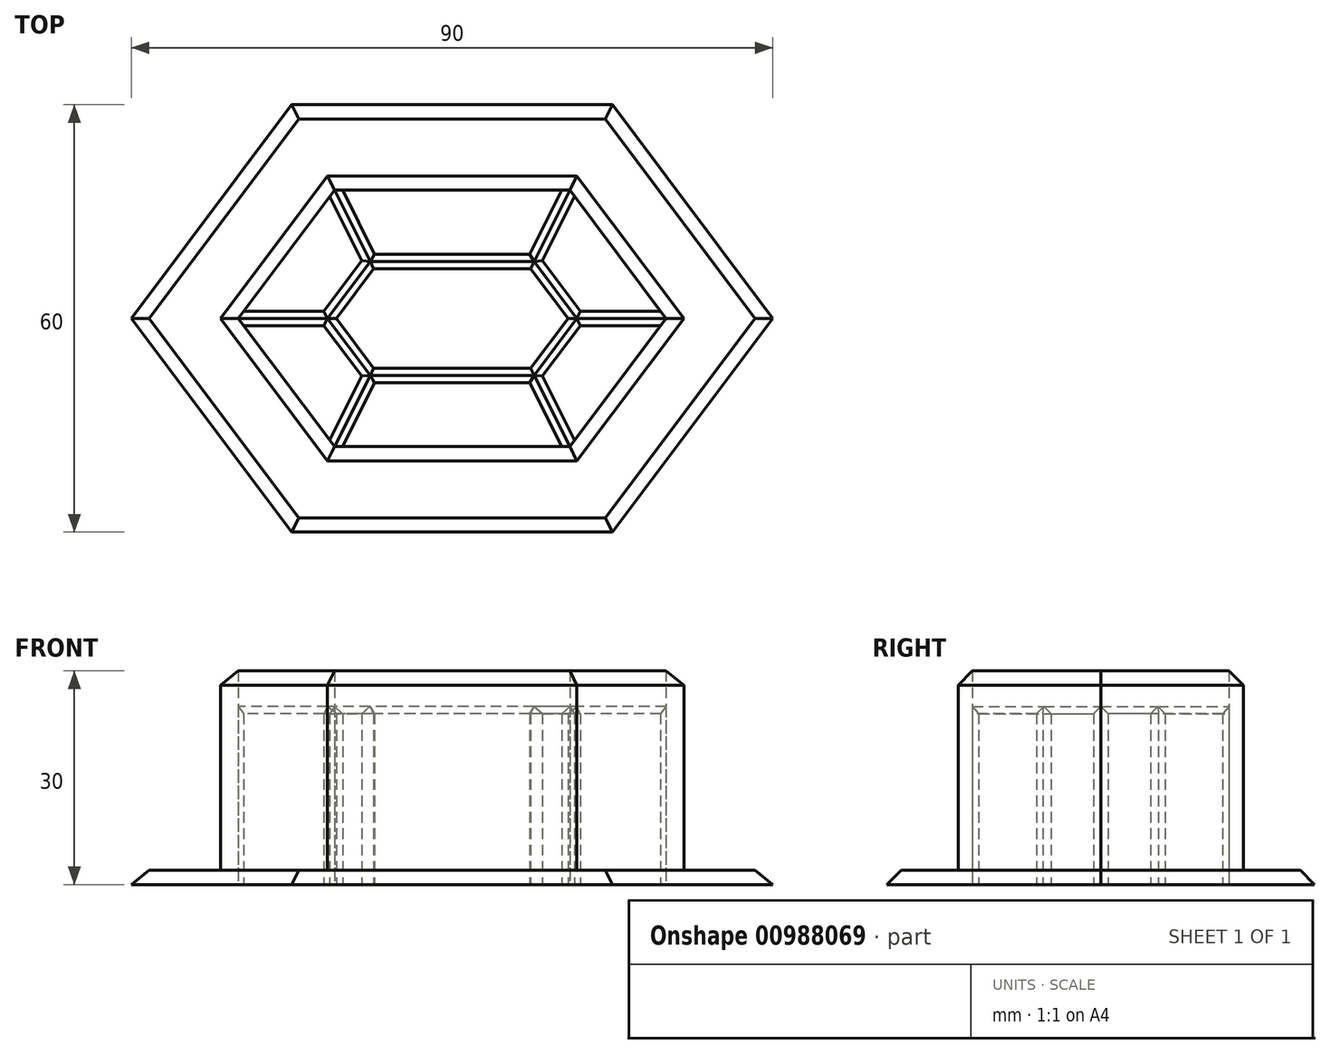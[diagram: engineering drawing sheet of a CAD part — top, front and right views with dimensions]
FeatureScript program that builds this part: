
annotation { "Feature Type Name" : "Feature", "Feature Type Description" : "" }
export const myFeature = defineFeature(function(context is Context, id is Id, definition is map)
    precondition{}
    {
        {
            var Q0;
            Q0=qCreatedBy(makeId("Top.planeOp"),FACE);
            var sketch = newSketch(context, id + "F0", { "sketchPlane" : qUnion([Q0])});
            skLineSegment(sketch, "E0", {"start": v(-17.5, 20) * mm, "end": v(17.5, 20) * mm});
            skLineSegment(sketch, "E1", {"start": v(17.5, 20) * mm, "end": v(32.5, 0) * mm});
            skLineSegment(sketch, "E2", {"start": v(32.5, 0) * mm, "end": v(17.5, -20) * mm});
            skLineSegment(sketch, "E3", {"start": v(17.5, -20) * mm, "end": v(-17.5, -20) * mm});
            skLineSegment(sketch, "E4", {"start": v(-17.5, -20) * mm, "end": v(-32.5, 0) * mm});
            skLineSegment(sketch, "E5", {"start": v(-32.5, 0) * mm, "end": v(-17.5, 20) * mm});
            skLineSegment(sketch, "E6", {"start": v(-32.5, 0) * mm, "end": v(32.5, 0) * mm, "construction": true});
            skLineSegment(sketch, "E7", {"start": v(0, 0) * mm, "end": v(0, 20) * mm, "construction": true});
            skLineSegment(sketch, "E8", {"start": v(0, 0) * mm, "end": v(0, -20) * mm, "construction": true});
            skLineSegment(sketch, "E9.0", {"start": v(-16.5, -18) * mm, "end": v(-30, 0) * mm});
            skLineSegment(sketch, "E9.1", {"start": v(-16.5, 18) * mm, "end": v(16.5, 18) * mm});
            skLineSegment(sketch, "E9.2", {"start": v(16.5, 18) * mm, "end": v(30, 0) * mm});
            skLineSegment(sketch, "E9.3", {"start": v(-30, 0) * mm, "end": v(-16.5, 18) * mm});
            skLineSegment(sketch, "E9.4", {"start": v(30, 0) * mm, "end": v(16.5, -18) * mm});
            skLineSegment(sketch, "E9.5", {"start": v(16.5, -18) * mm, "end": v(-16.5, -18) * mm});
            skLineSegment(sketch, "E10.0", {"start": v(-22.5, -30) * mm, "end": v(-45, 0) * mm});
            skLineSegment(sketch, "E10.1", {"start": v(-22.5, 30) * mm, "end": v(22.5, 30) * mm});
            skLineSegment(sketch, "E10.2", {"start": v(22.5, 30) * mm, "end": v(45, 0) * mm});
            skLineSegment(sketch, "E10.3", {"start": v(-45, 0) * mm, "end": v(-22.5, 30) * mm});
            skLineSegment(sketch, "E10.4", {"start": v(45, 0) * mm, "end": v(22.5, -30) * mm});
            skLineSegment(sketch, "E10.5", {"start": v(22.5, -30) * mm, "end": v(-22.5, -30) * mm});
            skSolve(sketch);
        }
        {
            var Q0;
            Q0=makeQuery(id+"F0.imprint","IMPRINT",FACE,{"disambiguationData":[TD([[makeQuery(id+"F0.imprint","IMPRINT",EDGE,{"derivedFrom":sQuery(id+"F0.wireOp",EDGE,"E0")}),-1.0]])]});
            extrude(context, id + "F1", {"entities" : qUnion([Q0]), "depth" : 30 * mm, "offsetDistance" : 25 * mm});
        }
        {
            var Q0;
            Q0=makeQuery(id+"F0.imprint","IMPRINT",FACE,{"disambiguationData":[TD([[makeQuery(id+"F0.imprint","IMPRINT",EDGE,{"derivedFrom":sQuery(id+"F0.wireOp",EDGE,"E0")}),1.0]])]});
            extrude(context, id + "F2", {"entities" : qUnion([Q0]), "operationType" : NewBodyOperationType.ADD, "depth" : 2 * mm, "offsetDistance" : 25 * mm});
        }
        {
            var Q0;
            Q0=makeQuery(id+"F1.opExtrude","CAP_EDGE",EDGE,{"disambiguationData":[OSD([sQuery(id+"F0.wireOp",EDGE,"E5")])],"isStart":false});
            var Q1;
            Q1=makeQuery(id+"F1.opExtrude","CAP_EDGE",EDGE,{"disambiguationData":[OSD([sQuery(id+"F0.wireOp",EDGE,"E0")])],"isStart":false});
            var Q2;
            Q2=makeQuery(id+"F1.opExtrude","CAP_EDGE",EDGE,{"disambiguationData":[OSD([sQuery(id+"F0.wireOp",EDGE,"E1")])],"isStart":false});
            var Q3;
            Q3=makeQuery(id+"F1.opExtrude","CAP_EDGE",EDGE,{"disambiguationData":[OSD([sQuery(id+"F0.wireOp",EDGE,"E2")])],"isStart":false});
            var Q4;
            Q4=makeQuery(id+"F1.opExtrude","CAP_EDGE",EDGE,{"disambiguationData":[OSD([sQuery(id+"F0.wireOp",EDGE,"E3")])],"isStart":false});
            var Q5;
            Q5=makeQuery(id+"F1.opExtrude","CAP_EDGE",EDGE,{"disambiguationData":[OSD([sQuery(id+"F0.wireOp",EDGE,"E4")])],"isStart":false});
            var Q6;
            Q6=makeQuery(id+"F2.opExtrude","CAP_EDGE",EDGE,{"disambiguationData":[OSD([sQuery(id+"F0.wireOp",EDGE,"E10.5")])],"isStart":false});
            var Q7;
            Q7=makeQuery(id+"F2.opExtrude","CAP_EDGE",EDGE,{"disambiguationData":[OSD([sQuery(id+"F0.wireOp",EDGE,"E10.4")])],"isStart":false});
            var Q8;
            Q8=makeQuery(id+"F2.opExtrude","CAP_EDGE",EDGE,{"disambiguationData":[OSD([sQuery(id+"F0.wireOp",EDGE,"E10.2")])],"isStart":false});
            var Q9;
            Q9=makeQuery(id+"F2.opExtrude","CAP_EDGE",EDGE,{"disambiguationData":[OSD([sQuery(id+"F0.wireOp",EDGE,"E10.0")])],"isStart":false});
            var Q10;
            Q10=makeQuery(id+"F2.opExtrude","CAP_EDGE",EDGE,{"disambiguationData":[OSD([sQuery(id+"F0.wireOp",EDGE,"E10.3")])],"isStart":false});
            var Q11;
            Q11=makeQuery(id+"F2.opExtrude","CAP_EDGE",EDGE,{"disambiguationData":[OSD([sQuery(id+"F0.wireOp",EDGE,"E10.1")])],"isStart":false});
            chamfer(context, id + "F3", {"entities" : qUnion([Q0, Q1, Q2, Q3, Q4, Q5, Q6, Q7, Q8, Q9, Q10, Q11]), "width" : 2 * mm, "tangentPropagation" : true});
        }
        {
            var Q0;
            Q0=qCreatedBy(makeId("Top.planeOp"),FACE);
            var sketch = newSketch(context, id + "F4", { "sketchPlane" : qUnion([Q0])});
            skLineSegment(sketch, "E11", {"start": v(-32.5, 0) * mm, "end": v(-17.5, 20) * mm});
            skLineSegment(sketch, "E12", {"start": v(-17.5, 20) * mm, "end": v(17.5, 20) * mm});
            skLineSegment(sketch, "E13", {"start": v(17.5, 20) * mm, "end": v(32.5, 0) * mm});
            skLineSegment(sketch, "E14", {"start": v(32.5, 0) * mm, "end": v(17.5, -20) * mm});
            skLineSegment(sketch, "E15", {"start": v(17.5, -20) * mm, "end": v(-17.5, -20) * mm});
            skLineSegment(sketch, "E16", {"start": v(-17.5, -20) * mm, "end": v(-32.5, 0) * mm});
            skLineSegment(sketch, "E17.0", {"start": v(-16.5, -18) * mm, "end": v(-30, 0) * mm});
            skLineSegment(sketch, "E17.1", {"start": v(-16.5, 18) * mm, "end": v(16.5, 18) * mm});
            skLineSegment(sketch, "E17.2", {"start": v(16.5, 18) * mm, "end": v(30, 0) * mm});
            skLineSegment(sketch, "E17.3", {"start": v(-30, 0) * mm, "end": v(-16.5, 18) * mm});
            skLineSegment(sketch, "E17.4", {"start": v(30, 0) * mm, "end": v(16.5, -18) * mm});
            skLineSegment(sketch, "E17.5", {"start": v(16.5, -18) * mm, "end": v(-16.5, -18) * mm});
            skLineSegment(sketch, "E18.0", {"start": v(-11.5, -8) * mm, "end": v(-17.5, 0) * mm, "construction": true});
            skLineSegment(sketch, "E18.1", {"start": v(-11.5, 8) * mm, "end": v(11.5, 8) * mm, "construction": true});
            skLineSegment(sketch, "E18.2", {"start": v(11.5, 8) * mm, "end": v(17.5, 0) * mm, "construction": true});
            skLineSegment(sketch, "E18.3", {"start": v(-17.5, 0) * mm, "end": v(-11.5, 8) * mm, "construction": true});
            skLineSegment(sketch, "E18.4", {"start": v(17.5, 0) * mm, "end": v(11.5, -8) * mm, "construction": true});
            skLineSegment(sketch, "E18.5", {"start": v(11.5, -8) * mm, "end": v(-11.5, -8) * mm, "construction": true});
            skLineSegment(sketch, "E19", {"start": v(-11.5, 8) * mm, "end": v(-16.5, 18) * mm, "construction": true});
            skLineSegment(sketch, "E20", {"start": v(11.5, 8) * mm, "end": v(16.5, 18) * mm, "construction": true});
            skLineSegment(sketch, "E21", {"start": v(17.5, 0) * mm, "end": v(30, 0) * mm, "construction": true});
            skLineSegment(sketch, "E22", {"start": v(11.5, -8) * mm, "end": v(16.5, -18) * mm, "construction": true});
            skLineSegment(sketch, "E23", {"start": v(-11.5, -8) * mm, "end": v(-16.5, -18) * mm, "construction": true});
            skLineSegment(sketch, "E24", {"start": v(-17.5, 0) * mm, "end": v(-30, 0) * mm, "construction": true});
            skLineSegment(sketch, "E25.0", {"start": v(-12.67, 8.1) * mm, "end": v(-17.17, 17.1) * mm});
            skLineSegment(sketch, "E25.1", {"start": v(-18, 1) * mm, "end": v(-12.67, 8.1) * mm});
            skLineSegment(sketch, "E25.2", {"start": v(-18, 1) * mm, "end": v(-29.25, 1) * mm});
            skLineSegment(sketch, "E26.0", {"start": v(-10.88, 9) * mm, "end": v(-15.38, 18) * mm});
            skLineSegment(sketch, "E26.1", {"start": v(-10.88, 9) * mm, "end": v(10.88, 9) * mm});
            skLineSegment(sketch, "E26.2", {"start": v(10.88, 9) * mm, "end": v(15.38, 18) * mm});
            skLineSegment(sketch, "E27.0", {"start": v(18, 1) * mm, "end": v(29.25, 1) * mm});
            skLineSegment(sketch, "E27.1", {"start": v(12.67, 8.1) * mm, "end": v(18, 1) * mm});
            skLineSegment(sketch, "E27.2", {"start": v(12.67, 8.1) * mm, "end": v(17.17, 17.1) * mm});
            skLineSegment(sketch, "E28.0", {"start": v(18, -1) * mm, "end": v(29.25, -1) * mm});
            skLineSegment(sketch, "E28.1", {"start": v(18, -1) * mm, "end": v(12.67, -8.1) * mm});
            skLineSegment(sketch, "E28.2", {"start": v(12.67, -8.1) * mm, "end": v(17.17, -17.1) * mm});
            skLineSegment(sketch, "E29.0", {"start": v(-10.88, -9) * mm, "end": v(-15.38, -18) * mm});
            skLineSegment(sketch, "E29.1", {"start": v(10.88, -9) * mm, "end": v(-10.88, -9) * mm});
            skLineSegment(sketch, "E29.2", {"start": v(10.88, -9) * mm, "end": v(15.38, -18) * mm});
            skLineSegment(sketch, "E30.0", {"start": v(-12.67, -8.1) * mm, "end": v(-17.17, -17.1) * mm});
            skLineSegment(sketch, "E30.1", {"start": v(-12.67, -8.1) * mm, "end": v(-18, -1) * mm});
            skLineSegment(sketch, "E30.2", {"start": v(-18, -1) * mm, "end": v(-29.25, -1) * mm});
            skLineSegment(sketch, "E31.0", {"start": v(-16.25, 0) * mm, "end": v(-11, 7) * mm});
            skLineSegment(sketch, "E31.1", {"start": v(11, 7) * mm, "end": v(16.25, 0) * mm});
            skLineSegment(sketch, "E31.2", {"start": v(16.25, 0) * mm, "end": v(11, -7) * mm});
            skLineSegment(sketch, "E31.3", {"start": v(-11, 7) * mm, "end": v(11, 7) * mm});
            skLineSegment(sketch, "E31.4", {"start": v(11, -7) * mm, "end": v(-11, -7) * mm});
            skLineSegment(sketch, "E31.5", {"start": v(-11, -7) * mm, "end": v(-16.25, 0) * mm});
            skSolve(sketch);
        }
        {
            var Q0;
            {var subQ4=sQuery(id+"F4.wireOp",EDGE,"E25.0");Q0=makeQuery(id+"F4.imprint","IMPRINT",FACE,{"disambiguationData":[TD([[makeQuery(id+"F4.imprint","IMPRINT",EDGE,{"derivedFrom":subQ4}),-1.0]])]});}
            extrude(context, id + "F5", {"entities" : qUnion([Q0]), "depth" : 25 * mm, "offsetDistance" : 25 * mm});
        }
        {
            var Q0;
            Q0=makeQuery(id+"F5.opExtrude","CAP_EDGE",EDGE,{"disambiguationData":[OSD([sQuery(id+"F4.wireOp",EDGE,"E30.2")])],"isStart":false});
            var Q1;
            Q1=makeQuery(id+"F5.opExtrude","CAP_EDGE",EDGE,{"disambiguationData":[OSD([sQuery(id+"F4.wireOp",EDGE,"E25.2")])],"isStart":false});
            var Q2;
            Q2=makeQuery(id+"F5.opExtrude","CAP_EDGE",EDGE,{"disambiguationData":[OSD([sQuery(id+"F4.wireOp",EDGE,"E30.1")])],"isStart":false});
            var Q3;
            Q3=makeQuery(id+"F5.opExtrude","CAP_EDGE",EDGE,{"disambiguationData":[OSD([sQuery(id+"F4.wireOp",EDGE,"E31.5")])],"isStart":false});
            var Q4;
            Q4=makeQuery(id+"F5.opExtrude","CAP_EDGE",EDGE,{"disambiguationData":[OSD([sQuery(id+"F4.wireOp",EDGE,"E31.0")])],"isStart":false});
            var Q5;
            Q5=makeQuery(id+"F5.opExtrude","CAP_EDGE",EDGE,{"disambiguationData":[OSD([sQuery(id+"F4.wireOp",EDGE,"E25.1")])],"isStart":false});
            var Q6;
            Q6=makeQuery(id+"F5.opExtrude","CAP_EDGE",EDGE,{"disambiguationData":[OSD([sQuery(id+"F4.wireOp",EDGE,"E25.0")])],"isStart":false});
            var Q7;
            Q7=makeQuery(id+"F5.opExtrude","CAP_EDGE",EDGE,{"disambiguationData":[OSD([sQuery(id+"F4.wireOp",EDGE,"E26.0")])],"isStart":false});
            var Q8;
            Q8=makeQuery(id+"F5.opExtrude","CAP_EDGE",EDGE,{"disambiguationData":[OSD([sQuery(id+"F4.wireOp",EDGE,"E31.3")])],"isStart":false});
            var Q9;
            Q9=makeQuery(id+"F5.opExtrude","CAP_EDGE",EDGE,{"disambiguationData":[OSD([sQuery(id+"F4.wireOp",EDGE,"E26.1")])],"isStart":false});
            var Q10;
            Q10=makeQuery(id+"F5.opExtrude","CAP_EDGE",EDGE,{"disambiguationData":[OSD([sQuery(id+"F4.wireOp",EDGE,"E29.1")])],"isStart":false});
            var Q11;
            Q11=makeQuery(id+"F5.opExtrude","CAP_EDGE",EDGE,{"disambiguationData":[OSD([sQuery(id+"F4.wireOp",EDGE,"E31.4")])],"isStart":false});
            var Q12;
            Q12=makeQuery(id+"F5.opExtrude","CAP_EDGE",EDGE,{"disambiguationData":[OSD([sQuery(id+"F4.wireOp",EDGE,"E29.0")])],"isStart":false});
            var Q13;
            Q13=makeQuery(id+"F5.opExtrude","CAP_EDGE",EDGE,{"disambiguationData":[OSD([sQuery(id+"F4.wireOp",EDGE,"E30.0")])],"isStart":false});
            var Q14;
            Q14=makeQuery(id+"F5.opExtrude","CAP_EDGE",EDGE,{"disambiguationData":[OSD([sQuery(id+"F4.wireOp",EDGE,"E28.2")])],"isStart":false});
            var Q15;
            Q15=makeQuery(id+"F5.opExtrude","CAP_EDGE",EDGE,{"disambiguationData":[OSD([sQuery(id+"F4.wireOp",EDGE,"E29.2")])],"isStart":false});
            var Q16;
            Q16=makeQuery(id+"F5.opExtrude","CAP_EDGE",EDGE,{"disambiguationData":[OSD([sQuery(id+"F4.wireOp",EDGE,"E28.1")])],"isStart":false});
            var Q17;
            Q17=makeQuery(id+"F5.opExtrude","CAP_EDGE",EDGE,{"disambiguationData":[OSD([sQuery(id+"F4.wireOp",EDGE,"E31.2")])],"isStart":false});
            var Q18;
            Q18=makeQuery(id+"F5.opExtrude","CAP_EDGE",EDGE,{"disambiguationData":[OSD([sQuery(id+"F4.wireOp",EDGE,"E28.0")])],"isStart":false});
            var Q19;
            Q19=makeQuery(id+"F5.opExtrude","CAP_EDGE",EDGE,{"disambiguationData":[OSD([sQuery(id+"F4.wireOp",EDGE,"E27.0")])],"isStart":false});
            var Q20;
            Q20=makeQuery(id+"F5.opExtrude","CAP_EDGE",EDGE,{"disambiguationData":[OSD([sQuery(id+"F4.wireOp",EDGE,"E27.1")])],"isStart":false});
            var Q21;
            Q21=makeQuery(id+"F5.opExtrude","CAP_EDGE",EDGE,{"disambiguationData":[OSD([sQuery(id+"F4.wireOp",EDGE,"E31.1")])],"isStart":false});
            var Q22;
            Q22=makeQuery(id+"F5.opExtrude","CAP_EDGE",EDGE,{"disambiguationData":[OSD([sQuery(id+"F4.wireOp",EDGE,"E27.2")])],"isStart":false});
            var Q23;
            Q23=makeQuery(id+"F5.opExtrude","CAP_EDGE",EDGE,{"disambiguationData":[OSD([sQuery(id+"F4.wireOp",EDGE,"E26.2")])],"isStart":false});
            chamfer(context, id + "F6", {"entities" : qUnion([Q0, Q1, Q2, Q3, Q4, Q5, Q6, Q7, Q8, Q9, Q10, Q11, Q12, Q13, Q14, Q15, Q16, Q17, Q18, Q19, Q20, Q21, Q22, Q23]), "width" : 1 * mm, "tangentPropagation" : true});
        }
    });
